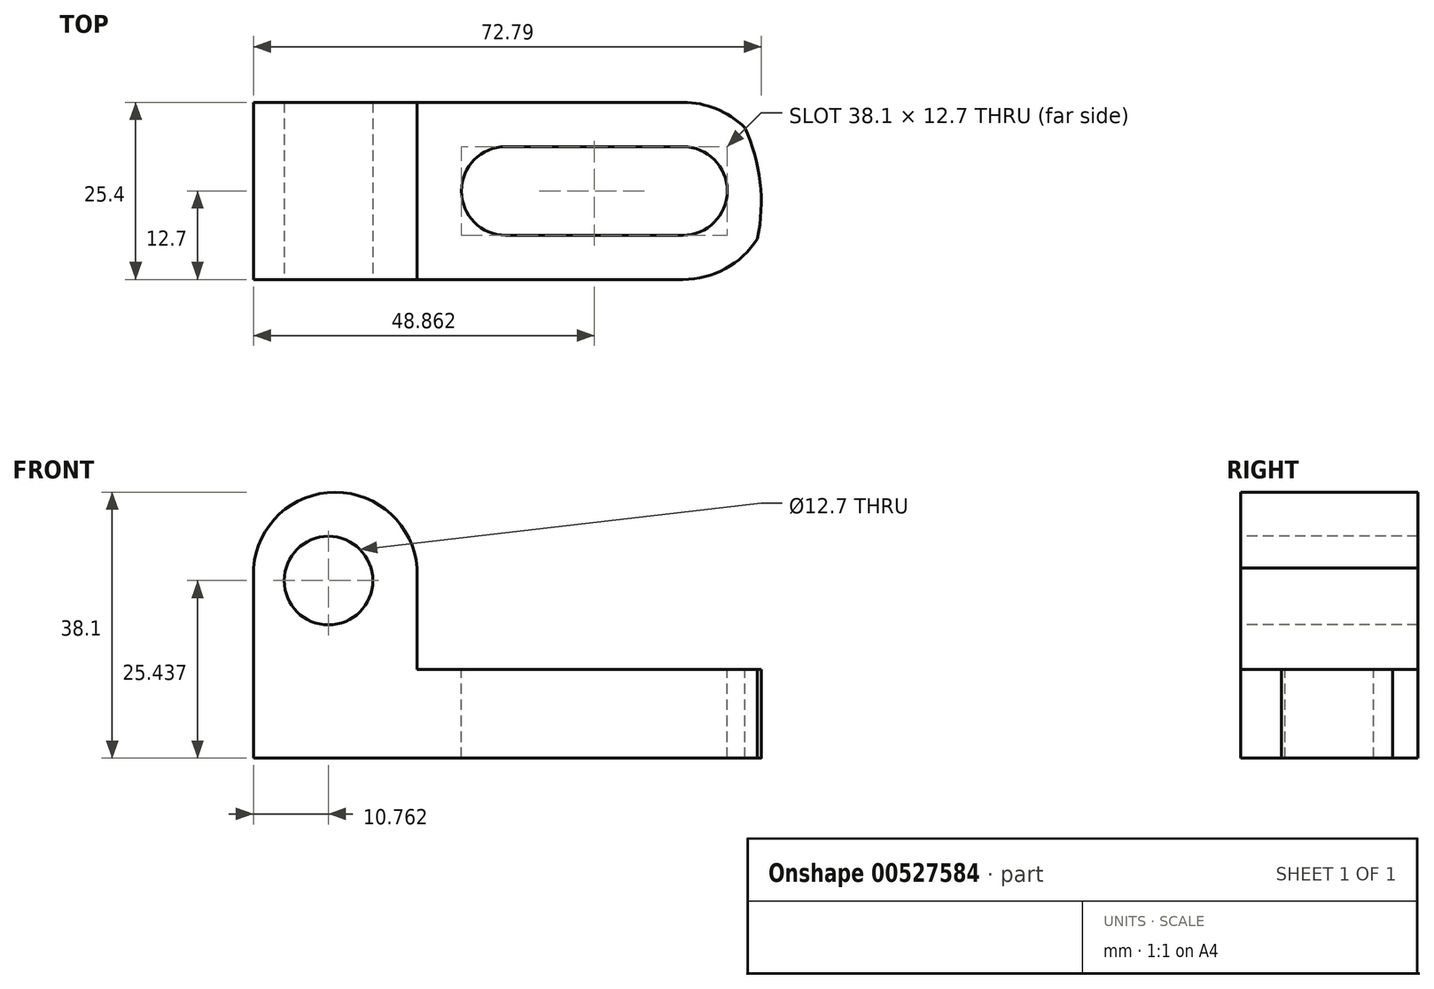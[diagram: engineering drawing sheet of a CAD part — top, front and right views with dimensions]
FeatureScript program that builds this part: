
annotation { "Feature Type Name" : "Feature", "Feature Type Description" : "" }
export const myFeature = defineFeature(function(context is Context, id is Id, definition is map)
    precondition{}
    {
        {
            var Q0;
            Q0=qCreatedBy(makeId("Front.planeOp"),FACE);
            var sketch = newSketch(context, id + "F0", { "sketchPlane" : qUnion([Q0])});
            skLineSegment(sketch, "E0", {"start": v(0, 0) * mm, "end": v(76.2, 0) * mm});
            skLineSegment(sketch, "E1", {"start": v(76.2, 0) * mm, "end": v(76.2, 12.7) * mm});
            skLineSegment(sketch, "E2", {"start": v(76.2, 12.7) * mm, "end": v(23.46, 12.7) * mm});
            skLineSegment(sketch, "E3", {"start": v(23.46, 12.7) * mm, "end": v(23.46, 38.1) * mm});
            skLineSegment(sketch, "E4", {"start": v(23.46, 38.1) * mm, "end": v(0, 38.1) * mm});
            skLineSegment(sketch, "E5", {"start": v(0, 38.1) * mm, "end": v(0, 0) * mm});
            skSolve(sketch);
        }
        {
            var Q0;
            Q0=makeQuery(id+"F0.imprint","IMPRINT",FACE,{"disambiguationData":[TD([[makeQuery(id+"F0.imprint","IMPRINT",EDGE,{"derivedFrom":sQuery(id+"F0.wireOp",EDGE,"E0")}),1.0]])]});
            extrude(context, id + "F1", {"entities" : qUnion([Q0]), "depth" : 25.4 * mm, "offsetDistance" : 25.4 * mm});
        }
        {
            var Q0;
            Q0=makeQuery(id+"F1.opExtrude","CAP_FACE",FACE,{"disambiguationData":[OSD([sQuery(id+"F0.wireOp",EDGE,"E0"),sQuery(id+"F0.wireOp",EDGE,"E1"),sQuery(id+"F0.wireOp",EDGE,"E2"),sQuery(id+"F0.wireOp",EDGE,"E3"),sQuery(id+"F0.wireOp",EDGE,"E4"),sQuery(id+"F0.wireOp",EDGE,"E5")])],"isStart":false});
            var sketch = newSketch(context, id + "F2", { "sketchPlane" : qUnion([Q0])});
            skCircle(sketch, "E6", {"center": v(10.76, 25.44) * mm, "radius": 6.35 * mm});
            skArc(sketch, "E7", {"start": v(23.46, 25.44) * mm, "mid": v(11.73, 38.1) * mm, "end": v(0, 25.44) * mm});
            skSolve(sketch);
        }
        {
            var Q0;
            {var subQ0=sQuery(id+"F2.wireOp",EDGE,"E7");var subQ1=makeQuery(id+"F1.opExtrude","CAP_EDGE",EDGE,{"disambiguationData":[OSD([sQuery(id+"F0.wireOp",EDGE,"E3")])],"isStart":false});var subQ2=makeQuery(id+"F2.imprint","INTERSECT",VERTEX,{"disambiguationData":[OD(1.0)],"derivedFrom":[subQ1,subQ0]});Q0=makeQuery(id+"F2.imprint","IMPRINT",FACE,{"disambiguationData":[TD([[makeQuery(id+"F2.imprint","IMPRINT",EDGE,{"disambiguationData":[TD([[subQ2,-1.0]])],"derivedFrom":subQ0}),-1.0]])]});}
            var Q1;
            {var subQ0=sQuery(id+"F2.wireOp",EDGE,"E7");var subQ1=makeQuery(id+"F1.opExtrude","CAP_EDGE",EDGE,{"disambiguationData":[OSD([sQuery(id+"F0.wireOp",EDGE,"E4")])],"isStart":false});var subQ2=makeQuery(id+"F2.imprint","INTERSECT",VERTEX,{"derivedFrom":[subQ1,subQ0]});Q1=makeQuery(id+"F2.imprint","IMPRINT",FACE,{"disambiguationData":[TD([[makeQuery(id+"F2.imprint","IMPRINT",EDGE,{"disambiguationData":[TD([[subQ2,-1.0]])],"derivedFrom":subQ0}),-1.0]])]});}
            var Q2;
            Q2=makeQuery(id+"F2.imprint","IMPRINT",FACE,{"disambiguationData":[TD([[makeQuery(id+"F2.imprint","IMPRINT",EDGE,{"derivedFrom":sQuery(id+"F2.wireOp",EDGE,"E6")}),1.0]])]});
            extrude(context, id + "F3", {"entities" : qUnion([Q0, Q1, Q2]), "operationType" : NewBodyOperationType.REMOVE, "oppositeDirection" : true, "depth" : 25.4 * mm, "offsetDistance" : 25.4 * mm});
        }
        {
            var Q0;
            Q0=makeQuery(id+"F1.opExtrude","SWEPT_FACE",FACE,{"disambiguationData":[OSD([sQuery(id+"F0.wireOp",EDGE,"E2")])]});
            var sketch = newSketch(context, id + "F4", { "sketchPlane" : qUnion([Q0])});
            skLineSegment(sketch, "E8", {"start": v(36.16, -6.35) * mm, "end": v(36.16, -19.05) * mm});
            skLineSegment(sketch, "E9", {"start": v(36.16, -19.05) * mm, "end": v(61.56, -19.05) * mm});
            skLineSegment(sketch, "E10", {"start": v(61.56, -19.05) * mm, "end": v(61.56, -6.35) * mm});
            skLineSegment(sketch, "E11", {"start": v(61.56, -6.35) * mm, "end": v(36.16, -6.35) * mm});
            skCircle(sketch, "E12", {"center": v(36.16, -12.7) * mm, "radius": 6.35 * mm});
            skCircle(sketch, "E13", {"center": v(61.56, -12.7) * mm, "radius": 6.35 * mm});
            skArc(sketch, "E14", {"start": v(61.56, -25.4) * mm, "mid": v(74.26, -12.7) * mm, "end": v(61.56, 0) * mm});
            skPoint(sketch, "E14.endSnap0", {"position": v(49.83, 0) * mm});
            skSolve(sketch);
        }
        {
            var Q0;
            {var subQ0=sQuery(id+"F4.wireOp",EDGE,"E10");Q0=makeQuery(id+"F4.imprint","IMPRINT",FACE,{"disambiguationData":[TD([[makeQuery(id+"F4.imprint","IMPRINT",EDGE,{"derivedFrom":subQ0}),-1.0]])]});}
            var Q1;
            {var subQ0=sQuery(id+"F4.wireOp",EDGE,"E8");Q1=makeQuery(id+"F4.imprint","IMPRINT",FACE,{"disambiguationData":[TD([[makeQuery(id+"F4.imprint","IMPRINT",EDGE,{"derivedFrom":subQ0}),1.0]])]});}
            var Q2;
            {var subQ0=sQuery(id+"F4.wireOp",EDGE,"E10");Q2=makeQuery(id+"F4.imprint","IMPRINT",FACE,{"disambiguationData":[TD([[makeQuery(id+"F4.imprint","IMPRINT",EDGE,{"derivedFrom":subQ0}),1.0]])]});}
            var Q3;
            {var subQ0=sQuery(id+"F4.wireOp",EDGE,"E9");Q3=makeQuery(id+"F4.imprint","IMPRINT",FACE,{"disambiguationData":[TD([[makeQuery(id+"F4.imprint","IMPRINT",EDGE,{"derivedFrom":subQ0}),1.0]])]});}
            var Q4;
            {var subQ0=sQuery(id+"F4.wireOp",EDGE,"E8");Q4=makeQuery(id+"F4.imprint","IMPRINT",FACE,{"disambiguationData":[TD([[makeQuery(id+"F4.imprint","IMPRINT",EDGE,{"derivedFrom":subQ0}),-1.0]])]});}
            var Q5;
            {var subQ0=sQuery(id+"F4.wireOp",EDGE,"E14");Q5=makeQuery(id+"F4.imprint","IMPRINT",FACE,{"disambiguationData":[TD([[makeQuery(id+"F4.imprint","IMPRINT",EDGE,{"derivedFrom":subQ0}),-1.0]])]});}
            extrude(context, id + "F5", {"entities" : qUnion([Q0, Q1, Q2, Q3, Q4, Q5]), "operationType" : NewBodyOperationType.REMOVE, "oppositeDirection" : true, "depth" : 25.4 * mm, "offsetDistance" : 25.4 * mm});
        }
        {
            var Q0;
            Q0=makeQuery(id+"F1.opExtrude","SWEPT_FACE",FACE,{"disambiguationData":[OSD([sQuery(id+"F0.wireOp",EDGE,"E2")])]});
            var sketch = newSketch(context, id + "F6", { "sketchPlane" : qUnion([Q0])});
            skArc(sketch, "E15", {"start": v(70.24, -25.4) * mm, "mid": v(72.72, -12.45) * mm, "end": v(68.38, 0) * mm});
            skSolve(sketch);
        }
        {
            var Q0;
            {var subQ0=sQuery(id+"F6.wireOp",EDGE,"E15");Q0=makeQuery(id+"F6.imprint","IMPRINT",FACE,{"disambiguationData":[TD([[makeQuery(id+"F6.imprint","IMPRINT",EDGE,{"derivedFrom":subQ0}),-1.0]])]});}
            extrude(context, id + "F7", {"entities" : qUnion([Q0]), "operationType" : NewBodyOperationType.REMOVE, "oppositeDirection" : true, "depth" : 25.4 * mm, "offsetDistance" : 25.4 * mm});
        }
    });
